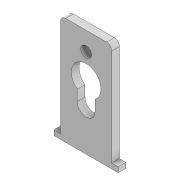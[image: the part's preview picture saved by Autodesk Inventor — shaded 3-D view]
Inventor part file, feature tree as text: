
AUTODESK INVENTOR PART (.ipt)
format: ipt  version: 2022 (Build 260153000, 153)  size: 118,272 bytes
history: native  units: mm
features: extrude x1, fillet x1, sketch x1
ambient origin geometry x8: Origin, YZ Plane, XZ Plane, XY Plane, X Axis, Y Axis, Z Axis, Center Point
bodies: Solid1 (feature_tree)
feature tree (3):
  extrude  "Extrusion1"  Depth=6.9mm
  fillet  "Fillet1"  Radius=18.0mm
  sketch  "Sketch1"  dims[d0=11.5mm d1=6.9mm d2=18.0mm d3=20.0mm d4=10.0mm d5=17.0mm d6=14.0mm d7=4.2mm d8=18.5mm d9=10.0mm d10=3.0mm d11=0.0mm d12=25.0mm d13=14.0mm d14=2.5mm d15=2.0mm d16=2.0mm]
